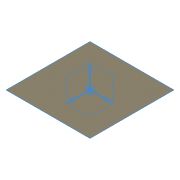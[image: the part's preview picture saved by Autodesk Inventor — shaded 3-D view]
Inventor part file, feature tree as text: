
AUTODESK INVENTOR PART (.ipt)
format: ipt  version: 2012 (Build 160160000, 160)  size: 78,336 bytes
history: native  units: in
note: dims shown in document units (in); Inventor stores cm internally (conversion verified against a paired STEP export)
features: extrude x1, shell x1, sketch x1
ambient origin geometry x8: Origin, YZ Plane, XZ Plane, XY Plane, X Axis, Y Axis, Z Axis, Center Point
bodies: Solid1 (feature_tree)
feature tree (3):
  extrude  "Extrusion1"  Depth=0.125in
  shell  "Shell1"  Thickness=120.0in
  sketch  "Sketch1"  dims[d0=120.0in d1=0.125in d2=120.0in d3=0.0in d4=0.01in]
